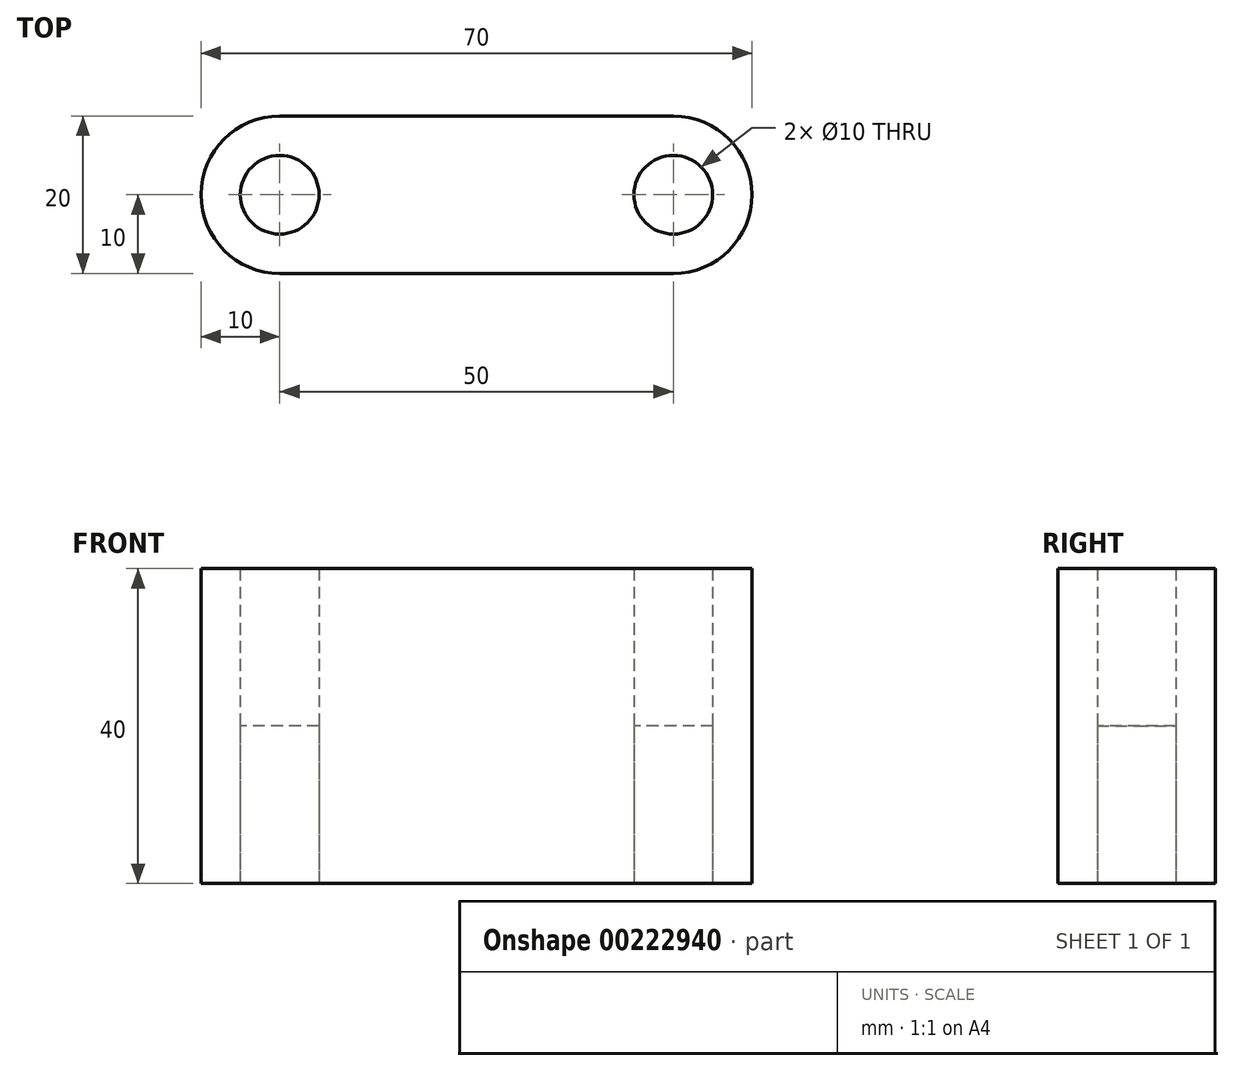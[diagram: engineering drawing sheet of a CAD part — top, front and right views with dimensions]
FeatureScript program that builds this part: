
annotation { "Feature Type Name" : "Feature", "Feature Type Description" : "" }
export const myFeature = defineFeature(function(context is Context, id is Id, definition is map)
    precondition{}
    {
        {
            var Q0;
            Q0=qCreatedBy(makeId("Top.planeOp"),FACE);
            var sketch = newSketch(context, id + "F0", { "sketchPlane" : qUnion([Q0])});
            skLineSegment(sketch, "E0.bottom", {"start": v(-25, -10) * mm, "end": v(25, -10) * mm});
            skLineSegment(sketch, "E0.top", {"start": v(-25, 10) * mm, "end": v(25, 10) * mm});
            skPoint(sketch, "E0.middle", {"position": v(0, 0) * mm});
            skCircle(sketch, "E1", {"center": v(-25, 0) * mm, "radius": 5 * mm});
            skCircle(sketch, "E2", {"center": v(25, 0) * mm, "radius": 5 * mm});
            skArc(sketch, "E3", {"start": v(-25, 10) * mm, "mid": v(-35, 0) * mm, "end": v(-25, -10) * mm});
            skArc(sketch, "E4", {"start": v(25, -10) * mm, "mid": v(35, 0) * mm, "end": v(25, 10) * mm});
            skSolve(sketch);
        }
        {
            var Q0;
            Q0=makeQuery(id+"F0.imprint","IMPRINT",FACE,{"disambiguationData":[TD([[makeQuery(id+"F0.imprint","IMPRINT",EDGE,{"derivedFrom":sQuery(id+"F0.wireOp",EDGE,"E2")}),1.0]])]});
            extrude(context, id + "F1", {"entities" : qUnion([Q0]), "depth" : 20 * mm});
        }
        {
            var Q0;
            Q0=makeQuery(id+"F0.imprint","IMPRINT",FACE,{"disambiguationData":[TD([[makeQuery(id+"F0.imprint","IMPRINT",EDGE,{"derivedFrom":sQuery(id+"F0.wireOp",EDGE,"E1")}),1.0]])]});
            extrude(context, id + "F2", {"entities" : qUnion([Q0]), "depth" : 20 * mm});
        }
        {
            var Q0;
            Q0=makeQuery(id+"F0.imprint","IMPRINT",FACE,{"disambiguationData":[TD([[makeQuery(id+"F0.imprint","IMPRINT",EDGE,{"derivedFrom":sQuery(id+"F0.wireOp",EDGE,"E0.top")}),-1.0]])]});
            extrude(context, id + "F3", {"entities" : qUnion([Q0]), "depth" : 40 * mm});
        }
    });
